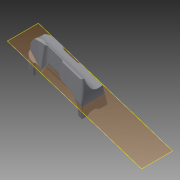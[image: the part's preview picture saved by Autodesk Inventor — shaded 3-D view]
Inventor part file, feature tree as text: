
AUTODESK INVENTOR PART (.ipt)
format: ipt  version: 2014 SP2 (Build 180246200, 246)  size: 1,041,920 bytes
history: native  units: in
note: dims shown in document units (in); Inventor stores cm internally (conversion verified against a paired STEP export)
features: sketch x19, projected_geometry x13, plane x7, extrude x6, loft x3, sweep x3, fillet x3, reference x3
ambient origin geometry x8: Origin, YZ Plane, XZ Plane, XY Plane, X Axis, Y Axis, Z Axis, Center Point
bodies: Solid1 (feature_tree)
feature tree (57):
  plane  "Work Plane2"
  sketch  "Sketch1"  dims[d0=-0.566in d1=0.005in]
  sketch  "Sketch2"  dims[d2=0.005in d3=0.005in]
  loft  "Loft1"
  sweep  "Sweep1"
  extrude  "Extrusion1"  Depth=0.0176in
  fillet  "Fillet2"  Radius=0.0176in
  sketch  "Sketch7"  dims[d17=0.226in d19=0.0in d20=0.235in]
  extrude  "Extrusion3"  TaperAngle=0.0deg  [1 undecoded]
  extrude  "Extrusion4"  Depth=0.026in
  sweep  "Sweep3"
  sketch  "Sketch11"  dims[d34=0.045in d36=0.35in]
  plane  "Work Plane3"
  loft  "Loft2"
  fillet  "Fillet3"  Radius=0.235in
  plane  "Work Plane5"
  extrude  "Extrusion5"  Depth=0.04in
  plane  "Work Plane6"
  extrude  "Extrusion6"  Depth=0.0345in
  plane  "Work Plane8"
  extrude  "Extrusion7"  Depth=1.0in TaperAngle=0.0deg
  sweep  "Sweep4"
  loft  "Loft3"
  fillet  "Fillet4"  Radius=0.325in
  plane  "Work Plane1"
  sketch  "Sketch3"  dims[d4=0.222in d5=0.0176in d6=0.0176in]
  reference  "Reference2"
  reference  "Reference3"
  sketch  "Sketch4"  dims[d7=0.0176in d10=0.0in d11=90.0deg]
  sketch  "Sketch5"  dims[d12=0.0in d13=90.0deg d14=0.026in]
  projected_geometry  "Projected Loop1"
  sketch  "Sketch6"  dims[d15=0.01in d16=0.2344in]
  sketch  "Sketch8"  dims[d21=1.0in d22=0.0in d24=0.04in]
  sketch  "Sketch9"  dims[d25=0.3285in d27=0.0345in]
  sketch  "Sketch10"  dims[d30=0.2656in d31=1.0in d32=0.0in]
  projected_geometry  "Projected Loop4"
  sketch  "Sketch12"  dims[d40=0.0in d41=1.0in d42=0.0in d43=0.325in]
  plane  "Work Plane4"
  sketch  "Sketch14"  dims[d44=0.23in]
  sketch  "Sketch15"  dims[d45=0.755in]
  sketch  "Sketch16"  dims[d46=0.252in]
  reference  "Reference4"
  sketch  "Sketch17"  dims[d47=0.545in]
  projected_geometry  "Projected Loop5"
  sketch  "Sketch19"  dims[d48=0.0in d49=90.0deg]
  projected_geometry  "Projected Loop7"
  sketch  "Sketch20"  dims[d50=0.0in d51=90.0deg]
  projected_geometry  "Projected Loop8"
  sketch  "Sketch21"  dims[d52=0.08in d53=90.0deg d54=-0.375in d58=0.232in d59=1.0in d60=0.0in d61=0.0in d62=0.4375in d63=0.0in d64=0.481in d65=1.0in d66=0.0in d67=0.026in d68=0.0in d69=0.0in d70=90.0deg d71=0.0in d72=90.0deg d73=0.01in]
  projected_geometry  "Projected Loop9"
  projected_geometry  "Project Cut Edges1"
  projected_geometry  "Project Cut Edges2"
  projected_geometry  "Project Cut Edges3"
  projected_geometry  "Project Cut Edges4"
  projected_geometry  "Project Cut Edges5"
  projected_geometry  "Project Cut Edges6"
  projected_geometry  "Project Cut Edges7"
note: 1 required parameter value undecoded (feature->parameter linkage not recoverable at this tier; creation-order binding heuristic only, values carry confidence <= 0.55)
